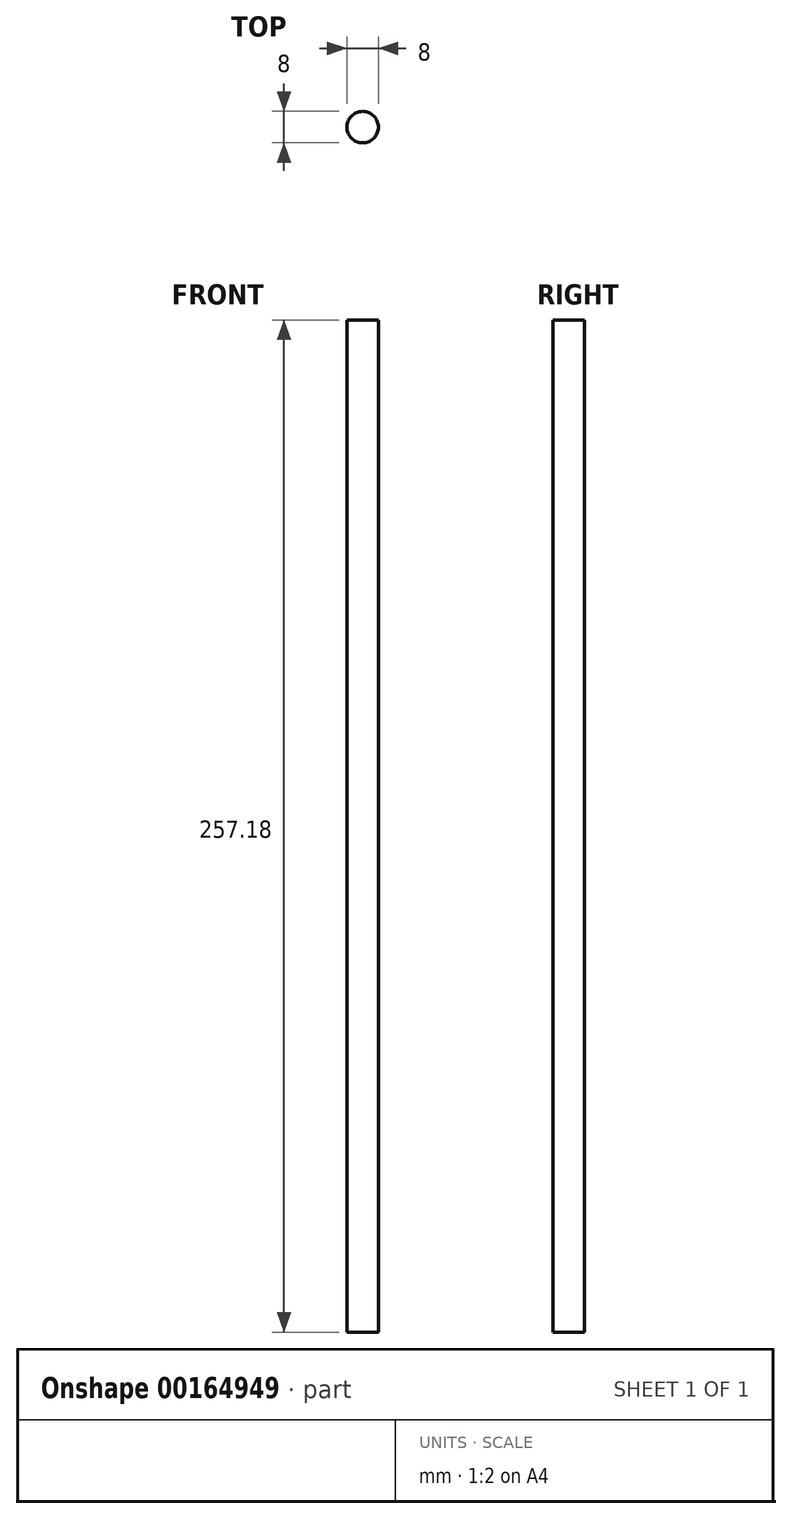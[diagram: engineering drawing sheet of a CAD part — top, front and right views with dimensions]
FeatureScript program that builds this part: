
annotation { "Feature Type Name" : "Feature", "Feature Type Description" : "" }
export const myFeature = defineFeature(function(context is Context, id is Id, definition is map)
    precondition{}
    {
        {
            var Q0;
            Q0=qCreatedBy(makeId("Top.planeOp"),FACE);
            var sketch = newSketch(context, id + "F0", { "sketchPlane" : qUnion([Q0])});
            skCircle(sketch, "E0", {"center": v(0, 0) * mm, "radius": 4 * mm});
            skSolve(sketch);
        }
        {
            var Q0;
            Q0=qSketchRegion(id+"F0",true);
            extrude(context, id + "F1", {"entities" : qUnion([Q0]), "depth" : 257.18 * mm});
        }
    });
